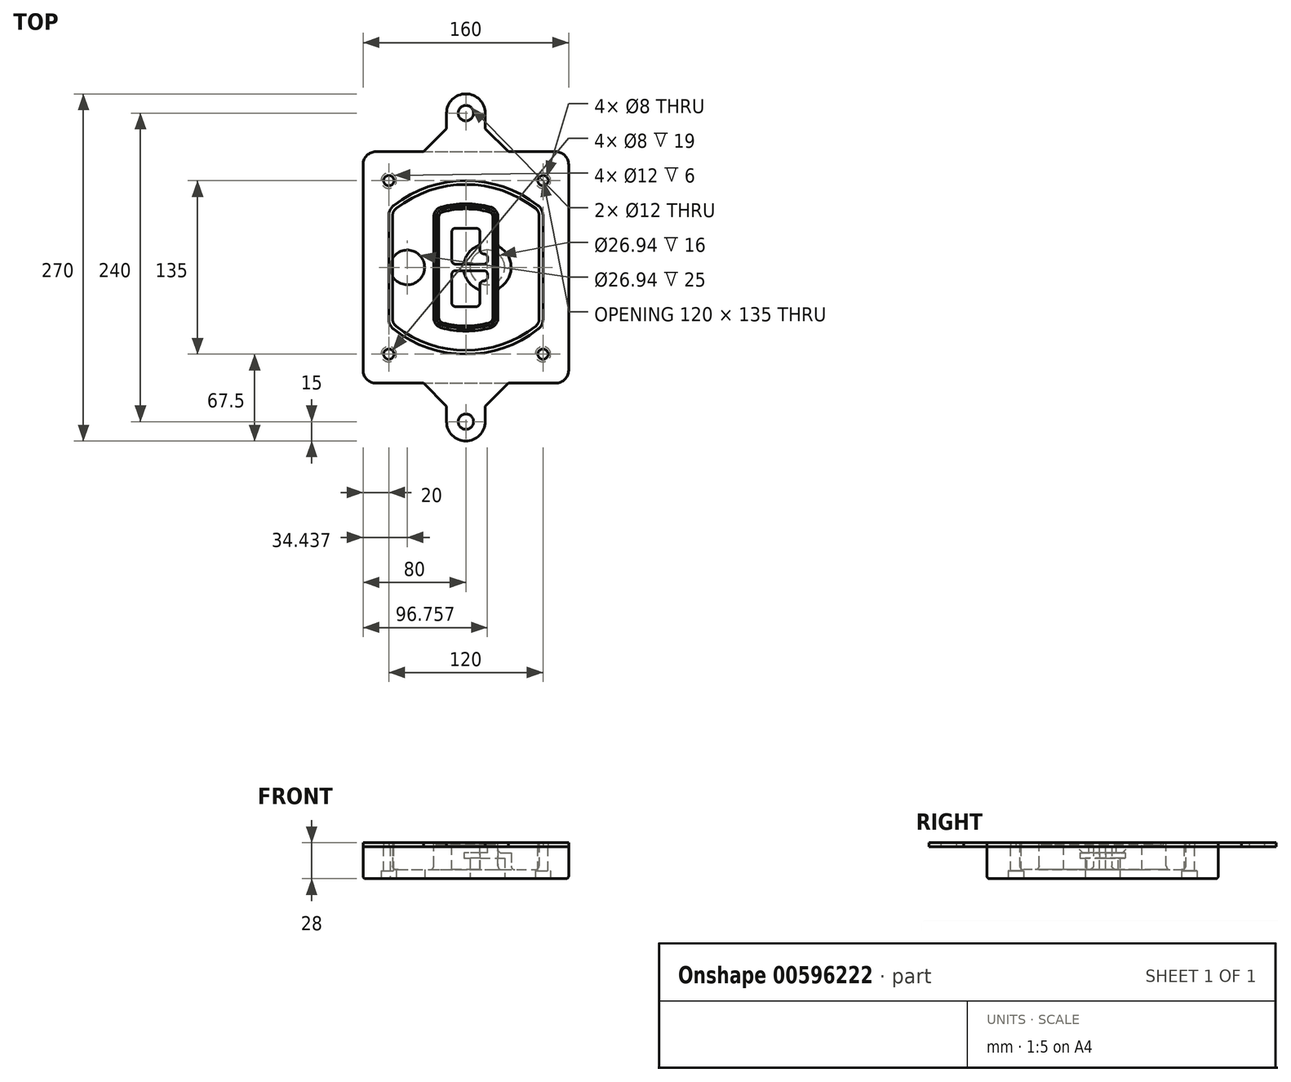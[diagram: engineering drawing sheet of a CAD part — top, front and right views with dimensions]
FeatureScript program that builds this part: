
annotation { "Feature Type Name" : "Feature", "Feature Type Description" : "" }
export const myFeature = defineFeature(function(context is Context, id is Id, definition is map)
    precondition{}
    {
        {
            var Q0;
            Q0=qCreatedBy(makeId("Top.planeOp"),FACE);
            var sketch = newSketch(context, id + "F0", { "sketchPlane" : qUnion([Q0])});
            skPoint(sketch, "E0.rect.middle", {"position": v(0, 0) * mm});
            skLineSegment(sketch, "E1.bottom", {"start": v(-70, -90) * mm, "end": v(70, -90) * mm});
            skLineSegment(sketch, "E1.top", {"start": v(-70, 90) * mm, "end": v(70, 90) * mm});
            skLineSegment(sketch, "E1.left", {"start": v(-80, -80) * mm, "end": v(-80, 80) * mm});
            skLineSegment(sketch, "E1.right", {"start": v(80, -80) * mm, "end": v(80, 80) * mm});
            skLineSegment(sketch, "E2", {"start": v(-80, 90) * mm, "end": v(80, -90) * mm, "construction": true});
            skLineSegment(sketch, "E3", {"start": v(80, 90) * mm, "end": v(-80, -90) * mm, "construction": true});
            skCircle(sketch, "E4", {"center": v(-60, 67.5) * mm, "radius": 4 * mm});
            skCircle(sketch, "E5", {"center": v(60, 67.5) * mm, "radius": 4 * mm});
            skCircle(sketch, "E6", {"center": v(60, -67.5) * mm, "radius": 4 * mm});
            skCircle(sketch, "E7", {"center": v(-60, -67.5) * mm, "radius": 4 * mm});
            skLineSegment(sketch, "E8", {"start": v(-60, 67.5) * mm, "end": v(60, 67.5) * mm, "construction": true});
            skLineSegment(sketch, "E9", {"start": v(60, 67.5) * mm, "end": v(60, -67.5) * mm, "construction": true});
            skLineSegment(sketch, "E10", {"start": v(60, -67.5) * mm, "end": v(-60, -67.5) * mm, "construction": true});
            skLineSegment(sketch, "E11", {"start": v(-60, -67.5) * mm, "end": v(-60, 67.5) * mm, "construction": true});
            skLineSegment(sketch, "E12", {"start": v(-60, 40.3) * mm, "end": v(-60, -40.3) * mm});
            skLineSegment(sketch, "E13", {"start": v(60, 40.3) * mm, "end": v(60, -40.3) * mm});
            skArc(sketch, "E14", {"start": v(56.15, 48.18) * mm, "mid": v(0, 67.5) * mm, "end": v(-56.15, 48.18) * mm});
            skArc(sketch, "E15", {"start": v(-56.15, -48.18) * mm, "mid": v(0, -67.5) * mm, "end": v(56.15, -48.18) * mm});
            skLineSegment(sketch, "E16", {"start": v(-60, 0) * mm, "end": v(60, 0) * mm, "construction": true});
            skPoint(sketch, "E17.visualSharp", {"position": v(-60, -45) * mm});
            skArc(sketch, "E17.filletArc", {"start": v(-60, -40.3) * mm, "mid": v(-58.99, -44.68) * mm, "end": v(-56.15, -48.18) * mm});
            skPoint(sketch, "E18.visualSharp", {"position": v(-60, 45) * mm});
            skArc(sketch, "E18.filletArc", {"start": v(-56.15, 48.18) * mm, "mid": v(-58.99, 44.68) * mm, "end": v(-60, 40.3) * mm});
            skPoint(sketch, "E19.visualSharp", {"position": v(60, 45) * mm});
            skArc(sketch, "E19.filletArc", {"start": v(60, 40.3) * mm, "mid": v(58.99, 44.68) * mm, "end": v(56.15, 48.18) * mm});
            skPoint(sketch, "E20.visualSharp", {"position": v(60, -45) * mm});
            skArc(sketch, "E20.filletArc", {"start": v(56.15, -48.18) * mm, "mid": v(58.99, -44.68) * mm, "end": v(60, -40.3) * mm});
            skPoint(sketch, "E21.visualSharp", {"position": v(-80, 90) * mm});
            skArc(sketch, "E21.filletArc", {"start": v(-70, 90) * mm, "mid": v(-77.07, 87.07) * mm, "end": v(-80, 80) * mm});
            skPoint(sketch, "E22.visualSharp", {"position": v(80, 90) * mm});
            skArc(sketch, "E22.filletArc", {"start": v(80, 80) * mm, "mid": v(77.07, 87.07) * mm, "end": v(70, 90) * mm});
            skPoint(sketch, "E23.visualSharp", {"position": v(80, -90) * mm});
            skArc(sketch, "E23.filletArc", {"start": v(70, -90) * mm, "mid": v(77.07, -87.07) * mm, "end": v(80, -80) * mm});
            skPoint(sketch, "E24.visualSharp", {"position": v(-80, -90) * mm});
            skArc(sketch, "E24.filletArc", {"start": v(-80, -80) * mm, "mid": v(-77.07, -87.07) * mm, "end": v(-70, -90) * mm});
            skArc(sketch, "E25.0", {"start": v(57, 40.3) * mm, "mid": v(56.3, 43.36) * mm, "end": v(54.3, 45.81) * mm});
            skLineSegment(sketch, "E25.1", {"start": v(57, 40.3) * mm, "end": v(57, -40.3) * mm});
            skArc(sketch, "E25.2", {"start": v(54.3, -45.81) * mm, "mid": v(56.3, -43.36) * mm, "end": v(57, -40.3) * mm});
            skArc(sketch, "E25.3", {"start": v(-54.3, -45.81) * mm, "mid": v(0, -64.5) * mm, "end": v(54.3, -45.81) * mm});
            skArc(sketch, "E25.4", {"start": v(-57, -40.3) * mm, "mid": v(-56.3, -43.36) * mm, "end": v(-54.3, -45.81) * mm});
            skArc(sketch, "E25.5", {"start": v(54.3, 45.81) * mm, "mid": v(0, 64.5) * mm, "end": v(-54.3, 45.81) * mm});
            skLineSegment(sketch, "E25.6", {"start": v(-57, 40.3) * mm, "end": v(-57, -40.3) * mm});
            skArc(sketch, "E25.7", {"start": v(-54.3, 45.81) * mm, "mid": v(-56.3, 43.36) * mm, "end": v(-57, 40.3) * mm});
            skArc(sketch, "E26.0", {"start": v(-58.62, 51.33) * mm, "mid": v(-62.58, 46.43) * mm, "end": v(-64, 40.3) * mm});
            skArc(sketch, "E26.1", {"start": v(58.62, 51.33) * mm, "mid": v(0, 71.5) * mm, "end": v(-58.62, 51.33) * mm});
            skArc(sketch, "E26.2", {"start": v(64, 40.3) * mm, "mid": v(62.58, 46.43) * mm, "end": v(58.62, 51.33) * mm});
            skLineSegment(sketch, "E26.3", {"start": v(64, 40.3) * mm, "end": v(64, -40.3) * mm});
            skArc(sketch, "E26.4", {"start": v(58.62, -51.33) * mm, "mid": v(62.58, -46.43) * mm, "end": v(64, -40.3) * mm});
            skLineSegment(sketch, "E26.5", {"start": v(-64, 40.3) * mm, "end": v(-64, -40.3) * mm});
            skArc(sketch, "E26.6", {"start": v(-58.62, -51.33) * mm, "mid": v(0, -71.5) * mm, "end": v(58.62, -51.33) * mm});
            skArc(sketch, "E26.7", {"start": v(-64, -40.3) * mm, "mid": v(-62.58, -46.43) * mm, "end": v(-58.62, -51.33) * mm});
            skSolve(sketch);
        }
        {
            var Q0;
            Q0=makeQuery(id+"F0.imprint","IMPRINT",FACE,{"disambiguationData":[TD([[makeQuery(id+"F0.imprint","IMPRINT",EDGE,{"derivedFrom":sQuery(id+"F0.wireOp",EDGE,"E1.bottom")}),1.0]])]});
            var Q1;
            Q1=makeQuery(id+"F0.imprint","IMPRINT",FACE,{"disambiguationData":[TD([[makeQuery(id+"F0.imprint","IMPRINT",EDGE,{"derivedFrom":sQuery(id+"F0.wireOp",EDGE,"E12")}),1.0]])]});
            var Q2;
            Q2=makeQuery(id+"F0.imprint","IMPRINT",FACE,{"disambiguationData":[TD([[makeQuery(id+"F0.imprint","IMPRINT",EDGE,{"derivedFrom":sQuery(id+"F0.wireOp",EDGE,"E25.0")}),1.0]])]});
            var Q3;
            Q3=makeQuery(id+"F0.imprint","IMPRINT",FACE,{"disambiguationData":[TD([[makeQuery(id+"F0.imprint","IMPRINT",EDGE,{"derivedFrom":sQuery(id+"F0.wireOp",EDGE,"E12")}),-1.0]])]});
            extrude(context, id + "F1", {"entities" : qUnion([Q0, Q1, Q2, Q3]), "oppositeDirection" : true, "depth" : 25 * mm});
        }
        {
            var Q0;
            Q0=makeQuery(id+"F0.imprint","IMPRINT",FACE,{"disambiguationData":[TD([[makeQuery(id+"F0.imprint","IMPRINT",EDGE,{"derivedFrom":sQuery(id+"F0.wireOp",EDGE,"E12")}),1.0]])]});
            extrude(context, id + "F2", {"entities" : qUnion([Q0]), "operationType" : NewBodyOperationType.ADD, "depth" : 3 * mm});
        }
        {
            var Q0;
            Q0=makeQuery(id+"F0.imprint","IMPRINT",FACE,{"disambiguationData":[TD([[makeQuery(id+"F0.imprint","IMPRINT",EDGE,{"derivedFrom":sQuery(id+"F0.wireOp",EDGE,"E25.0")}),1.0]])]});
            extrude(context, id + "F3", {"entities" : qUnion([Q0]), "operationType" : NewBodyOperationType.REMOVE, "oppositeDirection" : true, "depth" : 18 * mm});
        }
        {
            var Q0;
            Q0=makeQuery(id+"F2.opExtrude","CAP_FACE",FACE,{"disambiguationData":[OSD([sQuery(id+"F0.wireOp",EDGE,"E12"),sQuery(id+"F0.wireOp",EDGE,"E13"),sQuery(id+"F0.wireOp",EDGE,"E14"),sQuery(id+"F0.wireOp",EDGE,"E15"),sQuery(id+"F0.wireOp",EDGE,"E17.filletArc"),sQuery(id+"F0.wireOp",EDGE,"E18.filletArc"),sQuery(id+"F0.wireOp",EDGE,"E19.filletArc"),sQuery(id+"F0.wireOp",EDGE,"E20.filletArc"),sQuery(id+"F0.wireOp",EDGE,"E25.0"),sQuery(id+"F0.wireOp",EDGE,"E25.1"),sQuery(id+"F0.wireOp",EDGE,"E25.2"),sQuery(id+"F0.wireOp",EDGE,"E25.3"),sQuery(id+"F0.wireOp",EDGE,"E25.4"),sQuery(id+"F0.wireOp",EDGE,"E25.5"),sQuery(id+"F0.wireOp",EDGE,"E25.6"),sQuery(id+"F0.wireOp",EDGE,"E25.7")])],"isStart":false});
            var sketch = newSketch(context, id + "F4", { "sketchPlane" : qUnion([Q0])});
            skArc(sketch, "E27.0", {"start": v(-19.08, -46.97) * mm, "mid": v(0, -49.5) * mm, "end": v(19.08, -46.97) * mm});
            skArc(sketch, "E28.0", {"start": v(19.08, 46.97) * mm, "mid": v(0, 49.5) * mm, "end": v(-19.08, 46.97) * mm});
            skLineSegment(sketch, "E29", {"start": v(-25, 39.25) * mm, "end": v(-25, -39.25) * mm});
            skLineSegment(sketch, "E30", {"start": v(25, 39.25) * mm, "end": v(25, -39.25) * mm});
            skLineSegment(sketch, "E31", {"start": v(-25, 45.1) * mm, "end": v(25, 45.1) * mm, "construction": true});
            skLineSegment(sketch, "E32", {"start": v(-25, -45.1) * mm, "end": v(25, -45.1) * mm, "construction": true});
            skPoint(sketch, "E33.visualSharp", {"position": v(-25, 45.1) * mm});
            skArc(sketch, "E33.filletArc", {"start": v(-19.08, 46.97) * mm, "mid": v(-23.35, 44.11) * mm, "end": v(-25, 39.25) * mm});
            skPoint(sketch, "E34.visualSharp", {"position": v(25, 45.1) * mm});
            skArc(sketch, "E34.filletArc", {"start": v(25, 39.25) * mm, "mid": v(23.35, 44.11) * mm, "end": v(19.08, 46.97) * mm});
            skPoint(sketch, "E35.visualSharp", {"position": v(25, -45.1) * mm});
            skArc(sketch, "E35.filletArc", {"start": v(19.08, -46.97) * mm, "mid": v(23.35, -44.11) * mm, "end": v(25, -39.25) * mm});
            skPoint(sketch, "E36.visualSharp", {"position": v(-25, -45.1) * mm});
            skArc(sketch, "E36.filletArc", {"start": v(-25, -39.25) * mm, "mid": v(-23.35, -44.11) * mm, "end": v(-19.08, -46.97) * mm});
            skArc(sketch, "E37.0", {"start": v(54.3, 45.81) * mm, "mid": v(0, 64.5) * mm, "end": v(-54.3, 45.81) * mm});
            skArc(sketch, "E37.1", {"start": v(-54.3, 45.81) * mm, "mid": v(-56.3, 43.36) * mm, "end": v(-57, 40.3) * mm});
            skLineSegment(sketch, "E37.2", {"start": v(-57, 40.3) * mm, "end": v(-57, -40.3) * mm});
            skArc(sketch, "E37.3", {"start": v(-57, -40.3) * mm, "mid": v(-56.3, -43.36) * mm, "end": v(-54.3, -45.81) * mm});
            skArc(sketch, "E37.4", {"start": v(-54.3, -45.81) * mm, "mid": v(0, -64.5) * mm, "end": v(54.3, -45.81) * mm});
            skArc(sketch, "E37.5", {"start": v(54.3, -45.81) * mm, "mid": v(56.3, -43.36) * mm, "end": v(57, -40.3) * mm});
            skLineSegment(sketch, "E37.6", {"start": v(57, 40.3) * mm, "end": v(57, -40.3) * mm});
            skArc(sketch, "E37.7", {"start": v(57, 40.3) * mm, "mid": v(56.3, 43.36) * mm, "end": v(54.3, 45.81) * mm});
            skLineSegment(sketch, "E38.0", {"start": v(23, 39.25) * mm, "end": v(23, -39.25) * mm});
            skArc(sketch, "E38.1", {"start": v(18.56, -45.04) * mm, "mid": v(21.76, -42.9) * mm, "end": v(23, -39.25) * mm});
            skArc(sketch, "E38.2", {"start": v(-18.56, -45.04) * mm, "mid": v(0, -47.5) * mm, "end": v(18.56, -45.04) * mm});
            skArc(sketch, "E38.3", {"start": v(-23, -39.25) * mm, "mid": v(-21.76, -42.9) * mm, "end": v(-18.56, -45.04) * mm});
            skLineSegment(sketch, "E38.4", {"start": v(-23, 39.25) * mm, "end": v(-23, -39.25) * mm});
            skArc(sketch, "E38.5", {"start": v(23, 39.25) * mm, "mid": v(21.76, 42.9) * mm, "end": v(18.56, 45.04) * mm});
            skArc(sketch, "E38.6", {"start": v(-18.56, 45.04) * mm, "mid": v(-21.76, 42.9) * mm, "end": v(-23, 39.25) * mm});
            skArc(sketch, "E38.7", {"start": v(18.56, 45.04) * mm, "mid": v(0, 47.5) * mm, "end": v(-18.56, 45.04) * mm});
            skArc(sketch, "E39.0", {"start": v(21, 39.25) * mm, "mid": v(20.18, 41.68) * mm, "end": v(18.04, 43.1) * mm});
            skLineSegment(sketch, "E39.1", {"start": v(21, 39.25) * mm, "end": v(21, -39.25) * mm});
            skArc(sketch, "E39.2", {"start": v(18.04, -43.1) * mm, "mid": v(20.18, -41.68) * mm, "end": v(21, -39.25) * mm});
            skArc(sketch, "E39.3", {"start": v(-18.04, -43.1) * mm, "mid": v(0, -45.5) * mm, "end": v(18.04, -43.1) * mm});
            skArc(sketch, "E39.4", {"start": v(-21, -39.25) * mm, "mid": v(-20.18, -41.68) * mm, "end": v(-18.04, -43.1) * mm});
            skArc(sketch, "E39.5", {"start": v(18.04, 43.1) * mm, "mid": v(0, 45.5) * mm, "end": v(-18.04, 43.1) * mm});
            skLineSegment(sketch, "E39.6", {"start": v(-21, 39.25) * mm, "end": v(-21, -39.25) * mm});
            skArc(sketch, "E39.7", {"start": v(-18.04, 43.1) * mm, "mid": v(-20.18, 41.68) * mm, "end": v(-21, 39.25) * mm});
            skLineSegment(sketch, "E40", {"start": v(-25, 0) * mm, "end": v(25, 0) * mm, "construction": true});
            skLineSegment(sketch, "E41", {"start": v(-11, 5.5) * mm, "end": v(-11, 27.5) * mm});
            skLineSegment(sketch, "E42", {"start": v(-8, 30.5) * mm, "end": v(8, 30.5) * mm});
            skLineSegment(sketch, "E43", {"start": v(11, 27.5) * mm, "end": v(11, 13.5) * mm});
            skLineSegment(sketch, "E44", {"start": v(14, 10.5) * mm, "end": v(14, 10.5) * mm});
            skLineSegment(sketch, "E45", {"start": v(17, 7.5) * mm, "end": v(17, 5.5) * mm});
            skLineSegment(sketch, "E46", {"start": v(14, 2.5) * mm, "end": v(-8, 2.5) * mm});
            skPoint(sketch, "E47.visualSharp", {"position": v(-11, 30.5) * mm});
            skArc(sketch, "E47.filletArc", {"start": v(-8, 30.5) * mm, "mid": v(-10.12, 29.62) * mm, "end": v(-11, 27.5) * mm});
            skPoint(sketch, "E48.visualSharp", {"position": v(11, 30.5) * mm});
            skArc(sketch, "E48.filletArc", {"start": v(11, 27.5) * mm, "mid": v(10.12, 29.62) * mm, "end": v(8, 30.5) * mm});
            skPoint(sketch, "E49.visualSharp", {"position": v(11, 10.5) * mm});
            skArc(sketch, "E49.filletArc", {"start": v(11, 13.5) * mm, "mid": v(11.88, 11.38) * mm, "end": v(14, 10.5) * mm});
            skPoint(sketch, "E50.visualSharp", {"position": v(17, 10.5) * mm});
            skArc(sketch, "E50.filletArc", {"start": v(17, 7.5) * mm, "mid": v(16.12, 9.62) * mm, "end": v(14, 10.5) * mm});
            skPoint(sketch, "E51.visualSharp", {"position": v(17, 2.5) * mm});
            skArc(sketch, "E51.filletArc", {"start": v(14, 2.5) * mm, "mid": v(16.12, 3.38) * mm, "end": v(17, 5.5) * mm});
            skPoint(sketch, "E52.visualSharp", {"position": v(-11, 2.5) * mm});
            skArc(sketch, "E52.filletArc", {"start": v(-11, 5.5) * mm, "mid": v(-10.12, 3.38) * mm, "end": v(-8, 2.5) * mm});
            skLineSegment(sketch, "E53.0.MirrorCS", {"start": v(14, -2.5) * mm, "end": v(-8, -2.5) * mm});
            skArc(sketch, "E54.0.MirrorCS", {"start": v(-11, -5.5) * mm, "mid": v(-10.12, -3.38) * mm, "end": v(-8, -2.5) * mm});
            skLineSegment(sketch, "E55.0.MirrorCS", {"start": v(-11, -5.5) * mm, "end": v(-11, -27.5) * mm});
            skArc(sketch, "E56.0.MirrorCS", {"start": v(-8, -30.5) * mm, "mid": v(-10.12, -29.62) * mm, "end": v(-11, -27.5) * mm});
            skLineSegment(sketch, "E57.0.MirrorCS", {"start": v(-8, -30.5) * mm, "end": v(8, -30.5) * mm});
            skArc(sketch, "E58.0.MirrorCS", {"start": v(11, -27.5) * mm, "mid": v(10.12, -29.62) * mm, "end": v(8, -30.5) * mm});
            skLineSegment(sketch, "E59.0.MirrorCS", {"start": v(11, -27.5) * mm, "end": v(11, -13.5) * mm});
            skArc(sketch, "E60.0.MirrorCS", {"start": v(11, -13.5) * mm, "mid": v(11.88, -11.38) * mm, "end": v(14, -10.5) * mm});
            skArc(sketch, "E61.0.MirrorCS", {"start": v(17, -7.5) * mm, "mid": v(16.12, -9.62) * mm, "end": v(14, -10.5) * mm});
            skLineSegment(sketch, "E62.0.MirrorCS", {"start": v(17, -7.5) * mm, "end": v(17, -5.5) * mm});
            skArc(sketch, "E63.0.MirrorCS", {"start": v(14, -2.5) * mm, "mid": v(16.12, -3.38) * mm, "end": v(17, -5.5) * mm});
            skSolve(sketch);
        }
        {
            var Q0;
            Q0=makeQuery(id+"F4.imprint","IMPRINT",FACE,{"disambiguationData":[TD([[makeQuery(id+"F4.imprint","IMPRINT",EDGE,{"derivedFrom":sQuery(id+"F4.wireOp",EDGE,"E27.0")}),1.0]])]});
            var Q1;
            Q1=makeQuery(id+"F4.imprint","IMPRINT",FACE,{"disambiguationData":[TD([[makeQuery(id+"F4.imprint","IMPRINT",EDGE,{"derivedFrom":sQuery(id+"F4.wireOp",EDGE,"E38.0")}),-1.0]])]});
            var Q2;
            Q2=makeQuery(id+"F4.imprint","IMPRINT",FACE,{"disambiguationData":[TD([[makeQuery(id+"F4.imprint","IMPRINT",EDGE,{"derivedFrom":sQuery(id+"F4.wireOp",EDGE,"E39.0")}),1.0]])]});
            extrude(context, id + "F5", {"entities" : qUnion([Q0, Q1, Q2]), "operationType" : NewBodyOperationType.ADD, "endBound" : BoundingType.UP_TO_NEXT, "oppositeDirection" : true, "depth" : 25 * mm});
        }
        {
            var Q0;
            Q0=makeQuery(id+"F4.imprint","IMPRINT",FACE,{"disambiguationData":[TD([[makeQuery(id+"F4.imprint","IMPRINT",EDGE,{"derivedFrom":sQuery(id+"F4.wireOp",EDGE,"E38.0")}),-1.0]])]});
            extrude(context, id + "F6", {"entities" : qUnion([Q0]), "operationType" : NewBodyOperationType.REMOVE, "oppositeDirection" : true, "depth" : 2 * mm});
        }
        {
            var Q0;
            Q0=makeQuery(id+"F1.opExtrude","CAP_FACE",FACE,{"disambiguationData":[OSD([sQuery(id+"F0.wireOp",EDGE,"E1.bottom"),sQuery(id+"F0.wireOp",EDGE,"E1.top"),sQuery(id+"F0.wireOp",EDGE,"E1.left"),sQuery(id+"F0.wireOp",EDGE,"E1.right"),sQuery(id+"F0.wireOp",EDGE,"E4"),sQuery(id+"F0.wireOp",EDGE,"E5"),sQuery(id+"F0.wireOp",EDGE,"E6"),sQuery(id+"F0.wireOp",EDGE,"E7"),sQuery(id+"F0.wireOp",EDGE,"E21.filletArc"),sQuery(id+"F0.wireOp",EDGE,"E22.filletArc"),sQuery(id+"F0.wireOp",EDGE,"E23.filletArc"),sQuery(id+"F0.wireOp",EDGE,"E24.filletArc")])],"isStart":false});
            var sketch = newSketch(context, id + "F7", { "sketchPlane" : qUnion([Q0])});
            skCircle(sketch, "E64", {"center": v(16.76, 0) * mm, "radius": 13.47 * mm});
            skCircle(sketch, "E65", {"center": v(-45.56, 0) * mm, "radius": 13.47 * mm});
            skLineSegment(sketch, "E66", {"start": v(80, 0) * mm, "end": v(-80, 0) * mm});
            skCircle(sketch, "E67", {"center": v(16.76, 0) * mm, "radius": 18.47 * mm});
            skCircle(sketch, "E68", {"center": v(60, -67.5) * mm, "radius": 6 * mm});
            skCircle(sketch, "E69", {"center": v(-60, -67.5) * mm, "radius": 6 * mm});
            skCircle(sketch, "E70", {"center": v(-60, 67.5) * mm, "radius": 6 * mm});
            skCircle(sketch, "E71", {"center": v(60, 67.5) * mm, "radius": 6 * mm});
            skSolve(sketch);
        }
        {
            var Q0;
            {var subQ1=sQuery(id+"F7.wireOp",EDGE,"E66");var subQ4=sQuery(id+"F7.wireOp",EDGE,"E64");var subQ6=makeQuery(id+"F7.imprint","INTERSECT",VERTEX,{"disambiguationData":[OD(0.0)],"derivedFrom":[subQ4,subQ1]});Q0=makeQuery(id+"F7.imprint","IMPRINT",FACE,{"disambiguationData":[TD([[makeQuery(id+"F7.imprint","IMPRINT",EDGE,{"disambiguationData":[TD([[subQ6,-1.0]])],"derivedFrom":subQ4}),-1.0]])]});}
            var Q1;
            {var subQ0=sQuery(id+"F7.wireOp",EDGE,"E66");var subQ1=sQuery(id+"F7.wireOp",EDGE,"E64");var subQ3=makeQuery(id+"F7.imprint","INTERSECT",VERTEX,{"disambiguationData":[OD(0.0)],"derivedFrom":[subQ1,subQ0]});Q1=makeQuery(id+"F7.imprint","IMPRINT",FACE,{"disambiguationData":[TD([[makeQuery(id+"F7.imprint","IMPRINT",EDGE,{"disambiguationData":[TD([[subQ3,-1.0]])],"derivedFrom":subQ1}),1.0]])]});}
            var Q2;
            {var subQ0=sQuery(id+"F7.wireOp",EDGE,"E66");var subQ1=sQuery(id+"F7.wireOp",EDGE,"E64");var subQ3=makeQuery(id+"F7.imprint","INTERSECT",VERTEX,{"disambiguationData":[OD(0.0)],"derivedFrom":[subQ1,subQ0]});Q2=makeQuery(id+"F7.imprint","IMPRINT",FACE,{"disambiguationData":[TD([[makeQuery(id+"F7.imprint","IMPRINT",EDGE,{"disambiguationData":[TD([[subQ3,1.0]])],"derivedFrom":subQ1}),1.0]])]});}
            var Q3;
            {var subQ1=sQuery(id+"F7.wireOp",EDGE,"E66");var subQ4=sQuery(id+"F7.wireOp",EDGE,"E64");var subQ6=makeQuery(id+"F7.imprint","INTERSECT",VERTEX,{"disambiguationData":[OD(0.0)],"derivedFrom":[subQ4,subQ1]});Q3=makeQuery(id+"F7.imprint","IMPRINT",FACE,{"disambiguationData":[TD([[makeQuery(id+"F7.imprint","IMPRINT",EDGE,{"disambiguationData":[TD([[subQ6,1.0]])],"derivedFrom":subQ4}),-1.0]])]});}
            extrude(context, id + "F8", {"entities" : qUnion([Q0, Q1, Q2, Q3]), "operationType" : NewBodyOperationType.ADD, "oppositeDirection" : true, "depth" : 20 * mm});
        }
        {
            var Q0;
            {var subQ0=sQuery(id+"F7.wireOp",EDGE,"E66");var subQ1=sQuery(id+"F7.wireOp",EDGE,"E64");var subQ3=makeQuery(id+"F7.imprint","INTERSECT",VERTEX,{"disambiguationData":[OD(0.0)],"derivedFrom":[subQ1,subQ0]});Q0=makeQuery(id+"F7.imprint","IMPRINT",FACE,{"disambiguationData":[TD([[makeQuery(id+"F7.imprint","IMPRINT",EDGE,{"disambiguationData":[TD([[subQ3,-1.0]])],"derivedFrom":subQ1}),1.0]])]});}
            var Q1;
            {var subQ0=sQuery(id+"F7.wireOp",EDGE,"E66");var subQ1=sQuery(id+"F7.wireOp",EDGE,"E64");var subQ3=makeQuery(id+"F7.imprint","INTERSECT",VERTEX,{"disambiguationData":[OD(0.0)],"derivedFrom":[subQ1,subQ0]});Q1=makeQuery(id+"F7.imprint","IMPRINT",FACE,{"disambiguationData":[TD([[makeQuery(id+"F7.imprint","IMPRINT",EDGE,{"disambiguationData":[TD([[subQ3,1.0]])],"derivedFrom":subQ1}),1.0]])]});}
            extrude(context, id + "F9", {"entities" : qUnion([Q0, Q1]), "operationType" : NewBodyOperationType.REMOVE, "oppositeDirection" : true, "depth" : 16 * mm});
        }
        {
            var Q0;
            {var subQ0=sQuery(id+"F7.wireOp",EDGE,"E66");var subQ1=sQuery(id+"F7.wireOp",EDGE,"E65");var subQ3=makeQuery(id+"F7.imprint","INTERSECT",VERTEX,{"disambiguationData":[OD(0.0)],"derivedFrom":[subQ1,subQ0]});Q0=makeQuery(id+"F7.imprint","IMPRINT",FACE,{"disambiguationData":[TD([[makeQuery(id+"F7.imprint","IMPRINT",EDGE,{"disambiguationData":[TD([[subQ3,-1.0]])],"derivedFrom":subQ1}),1.0]])]});}
            var Q1;
            {var subQ0=sQuery(id+"F7.wireOp",EDGE,"E66");var subQ1=sQuery(id+"F7.wireOp",EDGE,"E65");var subQ3=makeQuery(id+"F7.imprint","INTERSECT",VERTEX,{"disambiguationData":[OD(0.0)],"derivedFrom":[subQ1,subQ0]});Q1=makeQuery(id+"F7.imprint","IMPRINT",FACE,{"disambiguationData":[TD([[makeQuery(id+"F7.imprint","IMPRINT",EDGE,{"disambiguationData":[TD([[subQ3,1.0]])],"derivedFrom":subQ1}),1.0]])]});}
            extrude(context, id + "F10", {"entities" : qUnion([Q0, Q1]), "operationType" : NewBodyOperationType.REMOVE, "oppositeDirection" : true, "depth" : 25 * mm});
        }
        {
            var Q0;
            Q0=makeQuery(id+"F7.imprint","IMPRINT",FACE,{"disambiguationData":[TD([[makeQuery(id+"F7.imprint","IMPRINT",EDGE,{"derivedFrom":sQuery(id+"F7.wireOp",EDGE,"E68")}),1.0]])]});
            var Q1;
            Q1=makeQuery(id+"F7.imprint","IMPRINT",FACE,{"disambiguationData":[TD([[makeQuery(id+"F7.imprint","IMPRINT",EDGE,{"derivedFrom":makeQuery(id+"F1.opExtrude","CAP_EDGE",EDGE,{"disambiguationData":[OSD([sQuery(id+"F0.wireOp",EDGE,"E5")])],"isStart":false})}),-1.0]])]});
            var Q2;
            Q2=makeQuery(id+"F7.imprint","IMPRINT",FACE,{"disambiguationData":[TD([[makeQuery(id+"F7.imprint","IMPRINT",EDGE,{"derivedFrom":sQuery(id+"F7.wireOp",EDGE,"E69")}),1.0]])]});
            var Q3;
            Q3=makeQuery(id+"F7.imprint","IMPRINT",FACE,{"disambiguationData":[TD([[makeQuery(id+"F7.imprint","IMPRINT",EDGE,{"derivedFrom":makeQuery(id+"F1.opExtrude","CAP_EDGE",EDGE,{"disambiguationData":[OSD([sQuery(id+"F0.wireOp",EDGE,"E4")])],"isStart":false})}),-1.0]])]});
            var Q4;
            Q4=makeQuery(id+"F7.imprint","IMPRINT",FACE,{"disambiguationData":[TD([[makeQuery(id+"F7.imprint","IMPRINT",EDGE,{"derivedFrom":sQuery(id+"F7.wireOp",EDGE,"E70")}),1.0]])]});
            var Q5;
            Q5=makeQuery(id+"F7.imprint","IMPRINT",FACE,{"disambiguationData":[TD([[makeQuery(id+"F7.imprint","IMPRINT",EDGE,{"derivedFrom":makeQuery(id+"F1.opExtrude","CAP_EDGE",EDGE,{"disambiguationData":[OSD([sQuery(id+"F0.wireOp",EDGE,"E7")])],"isStart":false})}),-1.0]])]});
            var Q6;
            Q6=makeQuery(id+"F7.imprint","IMPRINT",FACE,{"disambiguationData":[TD([[makeQuery(id+"F7.imprint","IMPRINT",EDGE,{"derivedFrom":sQuery(id+"F7.wireOp",EDGE,"E71")}),1.0]])]});
            var Q7;
            Q7=makeQuery(id+"F7.imprint","IMPRINT",FACE,{"disambiguationData":[TD([[makeQuery(id+"F7.imprint","IMPRINT",EDGE,{"derivedFrom":makeQuery(id+"F1.opExtrude","CAP_EDGE",EDGE,{"disambiguationData":[OSD([sQuery(id+"F0.wireOp",EDGE,"E6")])],"isStart":false})}),-1.0]])]});
            extrude(context, id + "F11", {"entities" : qUnion([Q0, Q1, Q2, Q3, Q4, Q5, Q6, Q7]), "operationType" : NewBodyOperationType.REMOVE, "oppositeDirection" : true, "depth" : 6 * mm, "offsetDistance" : 25 * mm});
        }
        {
            var Q0;
            Q0=makeQuery(id+"F9.boolean.opBoolean","COPY",FACE,{"derivedFrom":makeQuery(id+"F9.opExtrude","CAP_FACE",FACE,{"disambiguationData":[OSD([sQuery(id+"F7.wireOp",EDGE,"E64")])],"isStart":false})});
            var sketch = newSketch(context, id + "F12", { "sketchPlane" : qUnion([Q0])});
            skArc(sketch, "E72.0", {"start": v(11, 17.55) * mm, "mid": v(2.57, 11.82) * mm, "end": v(-1.54, 2.5) * mm});
            skArc(sketch, "E72.1", {"start": v(-1.54, -2.5) * mm, "mid": v(2.57, -11.82) * mm, "end": v(11, -17.55) * mm});
            skLineSegment(sketch, "E73", {"start": v(-1.54, -2.5) * mm, "end": v(14, -2.5) * mm});
            skLineSegment(sketch, "E74.0", {"start": v(14, 2.5) * mm, "end": v(-1.54, 2.5) * mm});
            skArc(sketch, "E74.1", {"start": v(14, 2.5) * mm, "mid": v(16.12, 3.38) * mm, "end": v(17, 5.5) * mm});
            skLineSegment(sketch, "E74.2", {"start": v(17, 7.5) * mm, "end": v(17, 5.5) * mm});
            skArc(sketch, "E74.3", {"start": v(17, 7.5) * mm, "mid": v(16.12, 9.62) * mm, "end": v(14, 10.5) * mm});
            skArc(sketch, "E74.4", {"start": v(11, 13.5) * mm, "mid": v(11.88, 11.38) * mm, "end": v(14, 10.5) * mm});
            skLineSegment(sketch, "E74.5", {"start": v(11, 17.55) * mm, "end": v(11, 13.5) * mm});
            skLineSegment(sketch, "E74.7", {"start": v(14, -2.5) * mm, "end": v(-1.54, -2.5) * mm});
            skArc(sketch, "E74.8", {"start": v(14, -2.5) * mm, "mid": v(16.12, -3.38) * mm, "end": v(17, -5.5) * mm});
            skLineSegment(sketch, "E74.9", {"start": v(17, -7.5) * mm, "end": v(17, -5.5) * mm});
            skArc(sketch, "E74.10", {"start": v(17, -7.5) * mm, "mid": v(16.12, -9.62) * mm, "end": v(14, -10.5) * mm});
            skArc(sketch, "E74.11", {"start": v(11, -13.5) * mm, "mid": v(11.88, -11.38) * mm, "end": v(14, -10.5) * mm});
            skLineSegment(sketch, "E74.12", {"start": v(11, -17.55) * mm, "end": v(11, -13.5) * mm});
            skPoint(sketch, "E75.orphan", {"position": v(11, -27.5) * mm});
            skPoint(sketch, "E76.orphan", {"position": v(-8, -2.5) * mm});
            skPoint(sketch, "E77.orphan", {"position": v(-8, 2.5) * mm});
            skPoint(sketch, "E78.orphan", {"position": v(11, 27.5) * mm});
            skSolve(sketch);
        }
        {
            var Q0;
            {var subQ7=sQuery(id+"F12.wireOp",EDGE,"E72.0");var subQ14=sQuery(id+"F12.wireOp",EDGE,"E72.1");var subQ16=sQuery(id+"F12.wireOp",EDGE,"E74.1");var subQ18=sQuery(id+"F12.wireOp",EDGE,"E74.8");Q0=qUnion([makeQuery(id+"F12.imprint","IMPRINT",FACE,{"disambiguationData":[TD([[makeQuery(id+"F12.imprint","IMPRINT",EDGE,{"derivedFrom":subQ7}),1.0]])]}),makeQuery(id+"F12.imprint","IMPRINT",FACE,{"disambiguationData":[TD([[makeQuery(id+"F12.imprint","IMPRINT",EDGE,{"derivedFrom":subQ14}),1.0]])]}),makeQuery(id+"F12.imprint","IMPRINT",FACE,{"disambiguationData":[TD([[makeQuery(id+"F12.imprint","IMPRINT",EDGE,{"derivedFrom":subQ16}),1.0]])]}),makeQuery(id+"F12.imprint","IMPRINT",FACE,{"disambiguationData":[TD([[makeQuery(id+"F12.imprint","IMPRINT",EDGE,{"derivedFrom":subQ18}),-1.0]])]})]);}
            var Q1;
            Q1=makeQuery(id+"F5.boolean.opBoolean","SPLIT",FACE,{"disambiguationData":[TD([makeQuery(id+"F5.opExtrude","SWEPT_FACE",FACE,{"disambiguationData":[OSD([sQuery(id+"F4.wireOp",EDGE,"E41")])]})])],"derivedFrom":makeQuery(id+"F3.boolean.opBoolean","COPY",FACE,{"derivedFrom":makeQuery(id+"F3.opExtrude","CAP_FACE",FACE,{"disambiguationData":[OSD([sQuery(id+"F0.wireOp",EDGE,"E25.0"),sQuery(id+"F0.wireOp",EDGE,"E25.1"),sQuery(id+"F0.wireOp",EDGE,"E25.2"),sQuery(id+"F0.wireOp",EDGE,"E25.3"),sQuery(id+"F0.wireOp",EDGE,"E25.4"),sQuery(id+"F0.wireOp",EDGE,"E25.5"),sQuery(id+"F0.wireOp",EDGE,"E25.6"),sQuery(id+"F0.wireOp",EDGE,"E25.7")])],"isStart":false})})});
            extrude(context, id + "F13", {"entities" : qUnion([Q0]), "operationType" : NewBodyOperationType.REMOVE, "endBound" : BoundingType.UP_TO_SURFACE, "endBoundEntityFace" : qUnion([Q1]), "depth" : 25 * mm});
        }
        {
            var Q0;
            Q0=makeQuery(id+"F3.boolean.opBoolean","COPY",EDGE,{"derivedFrom":makeQuery(id+"F3.opExtrude","CAP_EDGE",EDGE,{"disambiguationData":[OSD([sQuery(id+"F0.wireOp",EDGE,"E25.6")])],"isStart":false})});
            var Q1;
            Q1=makeQuery(id+"F8.boolean.opBoolean","INTERSECT",EDGE,{"derivedFrom":[makeQuery(id+"F5.opExtrude","SWEPT_FACE",FACE,{"disambiguationData":[OSD([sQuery(id+"F4.wireOp",EDGE,"E30")])]}),makeQuery(id+"F8.opExtrude","CAP_FACE",FACE,{"disambiguationData":[OSD([sQuery(id+"F7.wireOp",EDGE,"E67")])],"isStart":false})]});
            var Q2;
            Q2=makeQuery(id+"F8.boolean.opBoolean","INTERSECT",EDGE,{"disambiguationData":[OD(1.0)],"derivedFrom":[makeQuery(id+"F5.opExtrude","SWEPT_FACE",FACE,{"disambiguationData":[OSD([sQuery(id+"F4.wireOp",EDGE,"E30")])]}),makeQuery(id+"F8.opExtrude","SWEPT_FACE",FACE,{"disambiguationData":[OSD([sQuery(id+"F7.wireOp",EDGE,"E67")])]})]});
            var Q3;
            {var subQ0=sQuery(id+"F4.wireOp",EDGE,"E30");Q3=makeQuery(id+"F8.boolean.opBoolean","SPLIT",EDGE,{"disambiguationData":[TD([makeQuery(id+"F5.opExtrude","SWEPT_FACE",FACE,{"disambiguationData":[OSD([sQuery(id+"F4.wireOp",EDGE,"E35.filletArc")])]})])],"derivedFrom":makeQuery(id+"F5.opExtrude","CAP_EDGE",EDGE,{"disambiguationData":[OSD([subQ0])],"isStart":false})});}
            var Q4;
            {var subQ0=sQuery(id+"F0.wireOp",EDGE,"E25.7");var subQ1=sQuery(id+"F0.wireOp",EDGE,"E25.1");var subQ2=sQuery(id+"F0.wireOp",EDGE,"E25.6");var subQ3=sQuery(id+"F0.wireOp",EDGE,"E25.5");var subQ4=sQuery(id+"F0.wireOp",EDGE,"E25.4");var subQ5=sQuery(id+"F0.wireOp",EDGE,"E25.0");var subQ6=sQuery(id+"F0.wireOp",EDGE,"E25.2");var subQ7=sQuery(id+"F0.wireOp",EDGE,"E25.3");Q4=makeQuery(id+"F8.boolean.opBoolean","INTERSECT",EDGE,{"derivedFrom":[makeQuery(id+"F5.boolean.opBoolean","SPLIT",FACE,{"disambiguationData":[TD([makeQuery(id+"F2.opExtrude","SWEPT_FACE",FACE,{"disambiguationData":[OSD([subQ5])]})])],"derivedFrom":makeQuery(id+"F3.boolean.opBoolean","COPY",FACE,{"derivedFrom":makeQuery(id+"F3.opExtrude","CAP_FACE",FACE,{"disambiguationData":[OSD([subQ5,subQ1,subQ6,subQ7,subQ4,subQ3,subQ2,subQ0])],"isStart":false})})}),makeQuery(id+"F8.opExtrude","SWEPT_FACE",FACE,{"disambiguationData":[OSD([sQuery(id+"F7.wireOp",EDGE,"E67")])]})]});}
            var Q5;
            Q5=makeQuery(id+"F8.boolean.opBoolean","INTERSECT",EDGE,{"disambiguationData":[OD(0.0)],"derivedFrom":[makeQuery(id+"F5.opExtrude","SWEPT_FACE",FACE,{"disambiguationData":[OSD([sQuery(id+"F4.wireOp",EDGE,"E30")])]}),makeQuery(id+"F8.opExtrude","SWEPT_FACE",FACE,{"disambiguationData":[OSD([sQuery(id+"F7.wireOp",EDGE,"E67")])]})]});
            fillet(context, id + "F14", {"entities" : qUnion([Q0, Q1, Q2, Q3, Q4, Q5]), "radius" : 3 * mm, "tangentPropagation" : true, "allowEdgeOverflow" : false});
        }
        {
            var Q0;
            Q0=makeQuery(id+"F1.opExtrude","CAP_EDGE",EDGE,{"disambiguationData":[OSD([sQuery(id+"F0.wireOp",EDGE,"E1.bottom")])],"isStart":false});
            fillet(context, id + "F15", {"entities" : qUnion([Q0]), "radius" : 2 * mm, "tangentPropagation" : true, "allowEdgeOverflow" : false});
        }
        {
            var Q0;
            {var subQ0=sQuery(id+"F0.wireOp",EDGE,"E21.filletArc");var subQ1=sQuery(id+"F0.wireOp",EDGE,"E7");var subQ2=sQuery(id+"F0.wireOp",EDGE,"E6");var subQ3=sQuery(id+"F0.wireOp",EDGE,"E5");var subQ4=sQuery(id+"F0.wireOp",EDGE,"E4");var subQ5=sQuery(id+"F0.wireOp",EDGE,"E22.filletArc");var subQ6=sQuery(id+"F0.wireOp",EDGE,"E1.bottom");var subQ7=sQuery(id+"F0.wireOp",EDGE,"E1.right");var subQ8=sQuery(id+"F0.wireOp",EDGE,"E1.top");var subQ9=sQuery(id+"F0.wireOp",EDGE,"E1.left");var subQ10=sQuery(id+"F0.wireOp",EDGE,"E23.filletArc");var subQ11=sQuery(id+"F0.wireOp",EDGE,"E24.filletArc");Q0=makeQuery(id+"F2.boolean.opBoolean","SPLIT",FACE,{"disambiguationData":[TD([makeQuery(id+"F1.opExtrude","SWEPT_FACE",FACE,{"disambiguationData":[OSD([subQ6])]})])],"derivedFrom":makeQuery(id+"F1.opExtrude","CAP_FACE",FACE,{"disambiguationData":[OSD([subQ6,subQ8,subQ9,subQ7,subQ4,subQ3,subQ2,subQ1,subQ0,subQ5,subQ10,subQ11])],"isStart":true})});}
            var sketch = newSketch(context, id + "F16", { "sketchPlane" : qUnion([Q0])});
            skLineSegment(sketch, "E79", {"start": v(0, 90) * mm, "end": v(0, 139) * mm, "construction": true});
            skSolve(sketch);
        }
        {
            var Q0;
            Q0=makeQuery(id+"F16.imprint","IMPRINT",FACE,{"disambiguationData":[TD([[makeQuery(id+"F16.imprint","IMPRINT",EDGE,{"derivedFrom":makeQuery(id+"F1.opExtrude","CAP_EDGE",EDGE,{"disambiguationData":[OSD([sQuery(id+"F0.wireOp",EDGE,"E1.bottom")])],"isStart":true})}),1.0]])]});
            var sketch = newSketch(context, id + "F17", { "sketchPlane" : qUnion([Q0])});
            skCircle(sketch, "E80", {"center": v(0, 120) * mm, "radius": 6 * mm});
            skArc(sketch, "E81", {"start": v(-15, 120) * mm, "mid": v(0, 135) * mm, "end": v(15, 120) * mm});
            skLineSegment(sketch, "E82", {"start": v(-15, 108) * mm, "end": v(-15, 120) * mm});
            skLineSegment(sketch, "E83", {"start": v(15, 120) * mm, "end": v(15, 108) * mm});
            skLineSegment(sketch, "E84", {"start": v(15, 108) * mm, "end": v(33, 90) * mm});
            skLineSegment(sketch, "E85", {"start": v(-15, 108) * mm, "end": v(-33, 90) * mm});
            skLineSegment(sketch, "E86", {"start": v(-74.15, 0) * mm, "end": v(74.15, 0) * mm, "construction": true});
            skCircle(sketch, "E87.MirrorC", {"center": v(0, -120) * mm, "radius": 6 * mm});
            skLineSegment(sketch, "E88.MirrorCS", {"start": v(-15, -108) * mm, "end": v(-15, -120) * mm});
            skArc(sketch, "E89.MirrorCS", {"start": v(-15, -120) * mm, "mid": v(0, -135) * mm, "end": v(15, -120) * mm});
            skLineSegment(sketch, "E90.MirrorCS", {"start": v(15, -120) * mm, "end": v(15, -108) * mm});
            skLineSegment(sketch, "E91.MirrorCS", {"start": v(-15, -108) * mm, "end": v(-33, -90) * mm});
            skLineSegment(sketch, "E92.MirrorCS", {"start": v(15, -108) * mm, "end": v(33, -90) * mm});
            skSolve(sketch);
        }
        {
            var Q0;
            Q0=makeQuery(id+"F17.imprint","IMPRINT",FACE,{"disambiguationData":[TD([[makeQuery(id+"F17.imprint","IMPRINT",EDGE,{"derivedFrom":makeQuery(id+"F16.imprint","IMPRINT",EDGE,{"derivedFrom":makeQuery(id+"F1.opExtrude","CAP_EDGE",EDGE,{"disambiguationData":[OSD([sQuery(id+"F0.wireOp",EDGE,"E1.left")])],"isStart":true})})}),-1.0]])]});
            var Q1;
            {var subQ1=sQuery(id+"F17.wireOp",EDGE,"E91.MirrorCS");Q1=makeQuery(id+"F17.imprint","IMPRINT",FACE,{"disambiguationData":[TD([[makeQuery(id+"F17.imprint","IMPRINT",EDGE,{"derivedFrom":subQ1}),-1.0]])]});}
            var Q2;
            Q2=makeQuery(id+"F17.imprint","IMPRINT",FACE,{"disambiguationData":[TD([[makeQuery(id+"F17.imprint","IMPRINT",EDGE,{"derivedFrom":sQuery(id+"F17.wireOp",EDGE,"E80")}),-1.0]])]});
            var Q3;
            Q3=makeQuery(id+"F2.opExtrude","CAP_FACE",FACE,{"disambiguationData":[OSD([sQuery(id+"F0.wireOp",EDGE,"E12"),sQuery(id+"F0.wireOp",EDGE,"E13"),sQuery(id+"F0.wireOp",EDGE,"E14"),sQuery(id+"F0.wireOp",EDGE,"E15"),sQuery(id+"F0.wireOp",EDGE,"E17.filletArc"),sQuery(id+"F0.wireOp",EDGE,"E18.filletArc"),sQuery(id+"F0.wireOp",EDGE,"E19.filletArc"),sQuery(id+"F0.wireOp",EDGE,"E20.filletArc"),sQuery(id+"F0.wireOp",EDGE,"E25.0"),sQuery(id+"F0.wireOp",EDGE,"E25.1"),sQuery(id+"F0.wireOp",EDGE,"E25.2"),sQuery(id+"F0.wireOp",EDGE,"E25.3"),sQuery(id+"F0.wireOp",EDGE,"E25.4"),sQuery(id+"F0.wireOp",EDGE,"E25.5"),sQuery(id+"F0.wireOp",EDGE,"E25.6"),sQuery(id+"F0.wireOp",EDGE,"E25.7")])],"isStart":false});
            extrude(context, id + "F18", {"entities" : qUnion([Q0, Q1, Q2]), "endBound" : BoundingType.UP_TO_SURFACE, "depth" : 25 * mm, "endBoundEntityFace" : qUnion([Q3]), "offsetDistance" : 25 * mm});
        }
    });
